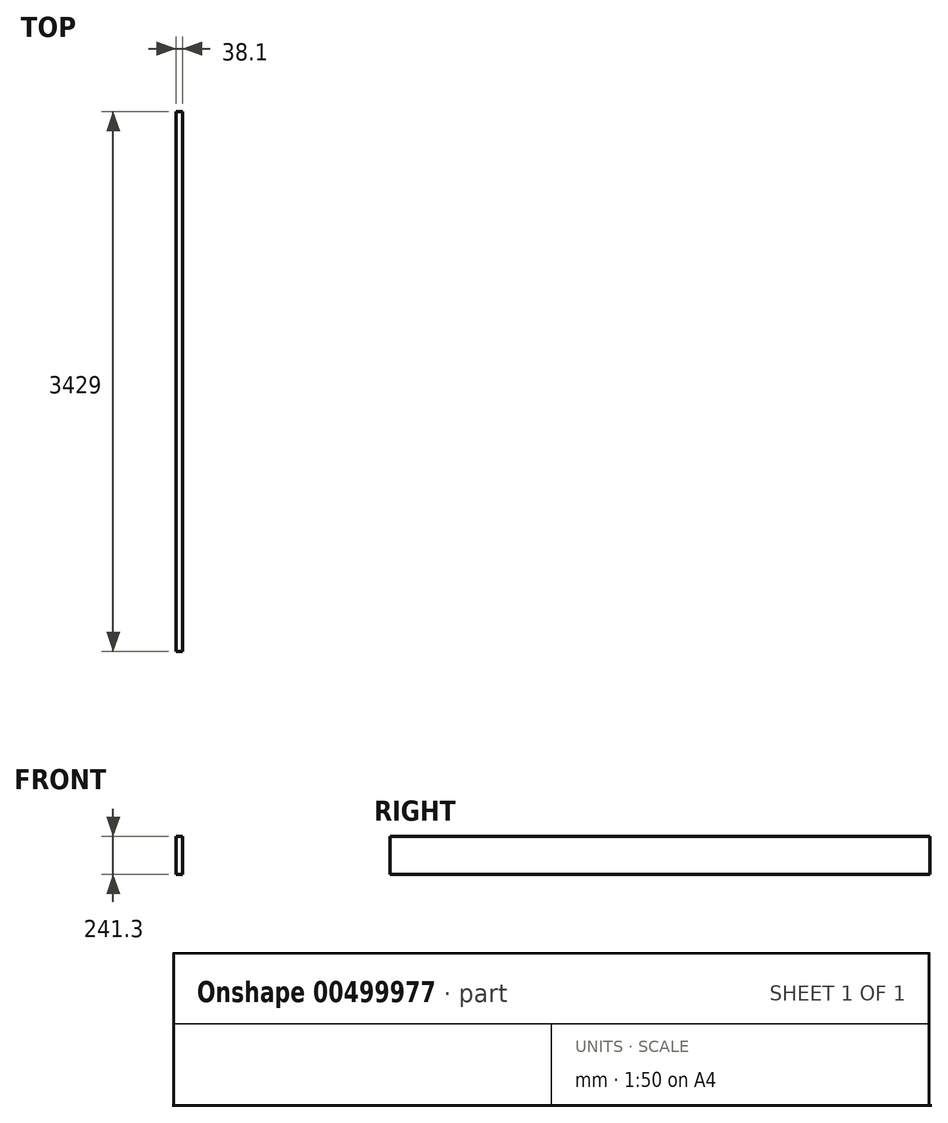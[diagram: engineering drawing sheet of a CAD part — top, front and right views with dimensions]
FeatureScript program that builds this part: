
annotation { "Feature Type Name" : "Feature", "Feature Type Description" : "" }
export const myFeature = defineFeature(function(context is Context, id is Id, definition is map)
    precondition{}
    {
        {
            var Q0;
            Q0=qCreatedBy(makeId("Right.planeOp"),FACE);
            var sketch = newSketch(context, id + "F0", { "sketchPlane" : qUnion([Q0])});
            skLineSegment(sketch, "E0.bottom", {"start": v(-1714.5, 120.65) * mm, "end": v(1714.5, 120.65) * mm});
            skLineSegment(sketch, "E0.top", {"start": v(-1714.5, -120.65) * mm, "end": v(1714.5, -120.65) * mm});
            skLineSegment(sketch, "E0.left", {"start": v(-1714.5, 120.65) * mm, "end": v(-1714.5, -120.65) * mm});
            skLineSegment(sketch, "E0.right", {"start": v(1714.5, 120.65) * mm, "end": v(1714.5, -120.65) * mm});
            skPoint(sketch, "E0.middle", {"position": v(0, 0) * mm});
            skSolve(sketch);
        }
        {
            var Q0;
            Q0=qSketchRegion(id+"F0",true);
            extrude(context, id + "F1", {"entities" : qUnion([Q0]), "depth" : 38.1 * mm, "offsetDistance" : 25.4 * mm});
        }
    });
